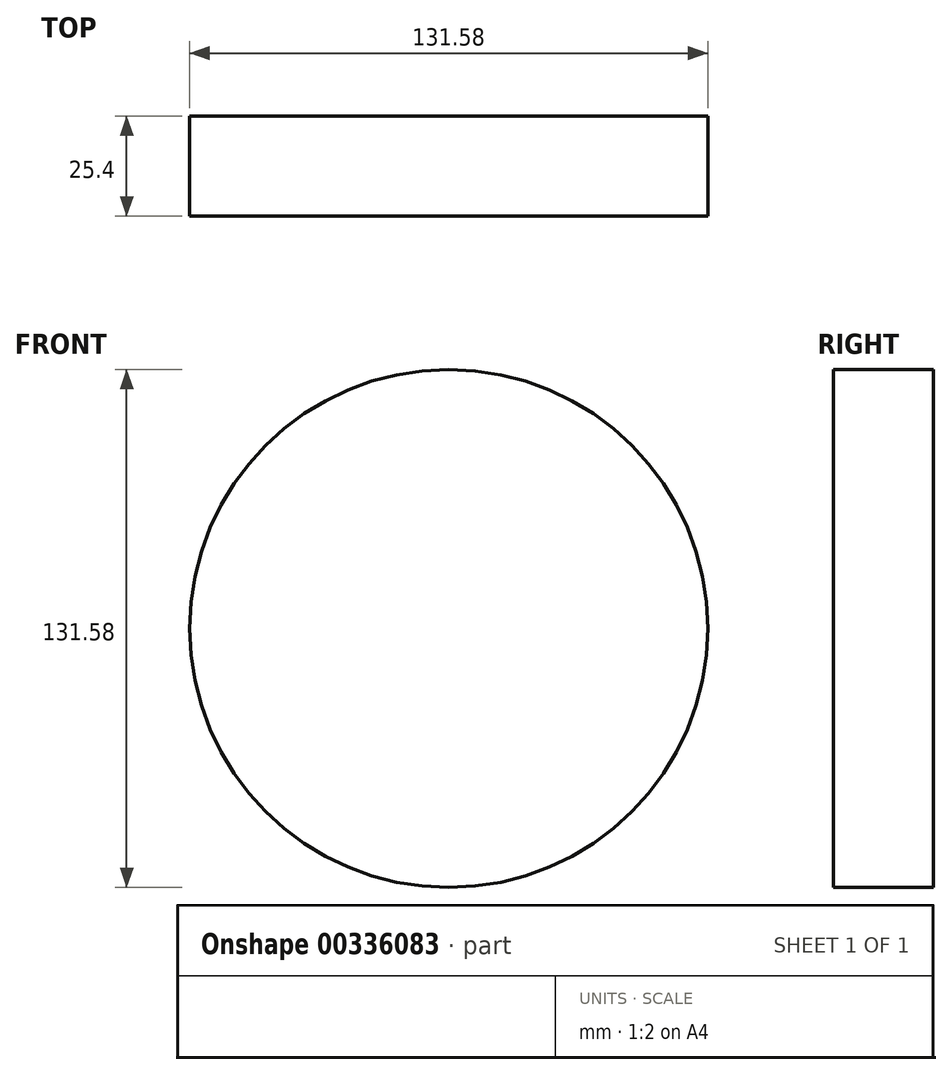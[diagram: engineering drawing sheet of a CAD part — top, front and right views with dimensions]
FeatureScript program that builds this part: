
annotation { "Feature Type Name" : "Feature", "Feature Type Description" : "" }
export const myFeature = defineFeature(function(context is Context, id is Id, definition is map)
    precondition{}
    {
        {
            var Q0;
            Q0=qCreatedBy(makeId("Front.planeOp"),FACE);
            var sketch = newSketch(context, id + "F0", { "sketchPlane" : qUnion([Q0])});
            skCircle(sketch, "E0", {"center": v(0, 0) * mm, "radius": 65.8 * mm});
            skSolve(sketch);
        }
        {
            var Q0;
            Q0 = qSketchRegion(id + "F0", true);
            extrude(context, id + "F1", {"entities" : qUnion([Q0]), "depth" : 25.4 * mm});
        }
    });
